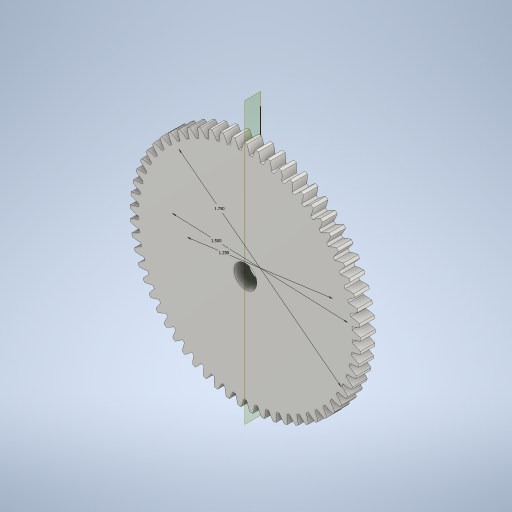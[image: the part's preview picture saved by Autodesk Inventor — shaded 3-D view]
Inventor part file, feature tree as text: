
AUTODESK INVENTOR PART (.ipt)
format: ipt  version: 2024 (Build 280153000, 153)  size: 913,920 bytes
history: native  units: mm (DEFAULTED — no unit token found)
features: sketch x5, plane x4, extrude x3, other x3, revolve x1
ambient origin geometry x8: Origin, YZ Plane, XZ Plane, XY Plane, X Axis, Y Axis, Z Axis, Center Point
bodies: Solid1 (feature_tree)
feature tree (16):
  extrude  "Extrusion1"  Depth=3.175mm TaperAngle=0.0deg
  plane  "Work Plane1"
  plane  "Work Plane2"
  plane  "Work Plane3"
  other  "Spur Gear"
  extrude  "Extrusion2"  Depth=76.2mm TaperAngle=0.0deg
  sketch  "Sketch4"  dims[d6=0.0mm d7=0.515015mm d9=0.0mm]
  plane  "Work Plane4"
  revolve  "Revolution1"  [1 undecoded]
  extrude  "Extrusion3"  TaperAngle=0.0deg  [1 undecoded]
  sketch  "Sketch1"  dims[d0=50.0761mm d1=3.175mm d2=0.0mm]
  other  "Srf1"
  sketch  "Sketch3"  dims[d3=48.41875mm d4=76.2mm d5=0.0mm]
  sketch  "Sketch5"  dims[d14=0.0mm d15=32.1818mm d16=0.0mm]
  sketch  "Sketch6"  dims[d17=0.0mm d18=0.0mm d19=32.1818mm d20=5.0mm d21=25.4mm d22=0.0mm d23=44.45mm d24=38.1mm d25=31.75mm d26=90.0deg d27=1.5875mm d28=1.5875mm d29=360.0deg d30=1.5875mm d31=0.79375mm d32=0.1524mm d33=2.54mm d35=500.0mm d37=360.0deg d39=1.5875mm d40=0.0mm]
  other  "Pitch Diameter"
note: 2 required parameter values undecoded (feature->parameter linkage not recoverable at this tier; creation-order binding heuristic only, values carry confidence <= 0.55)